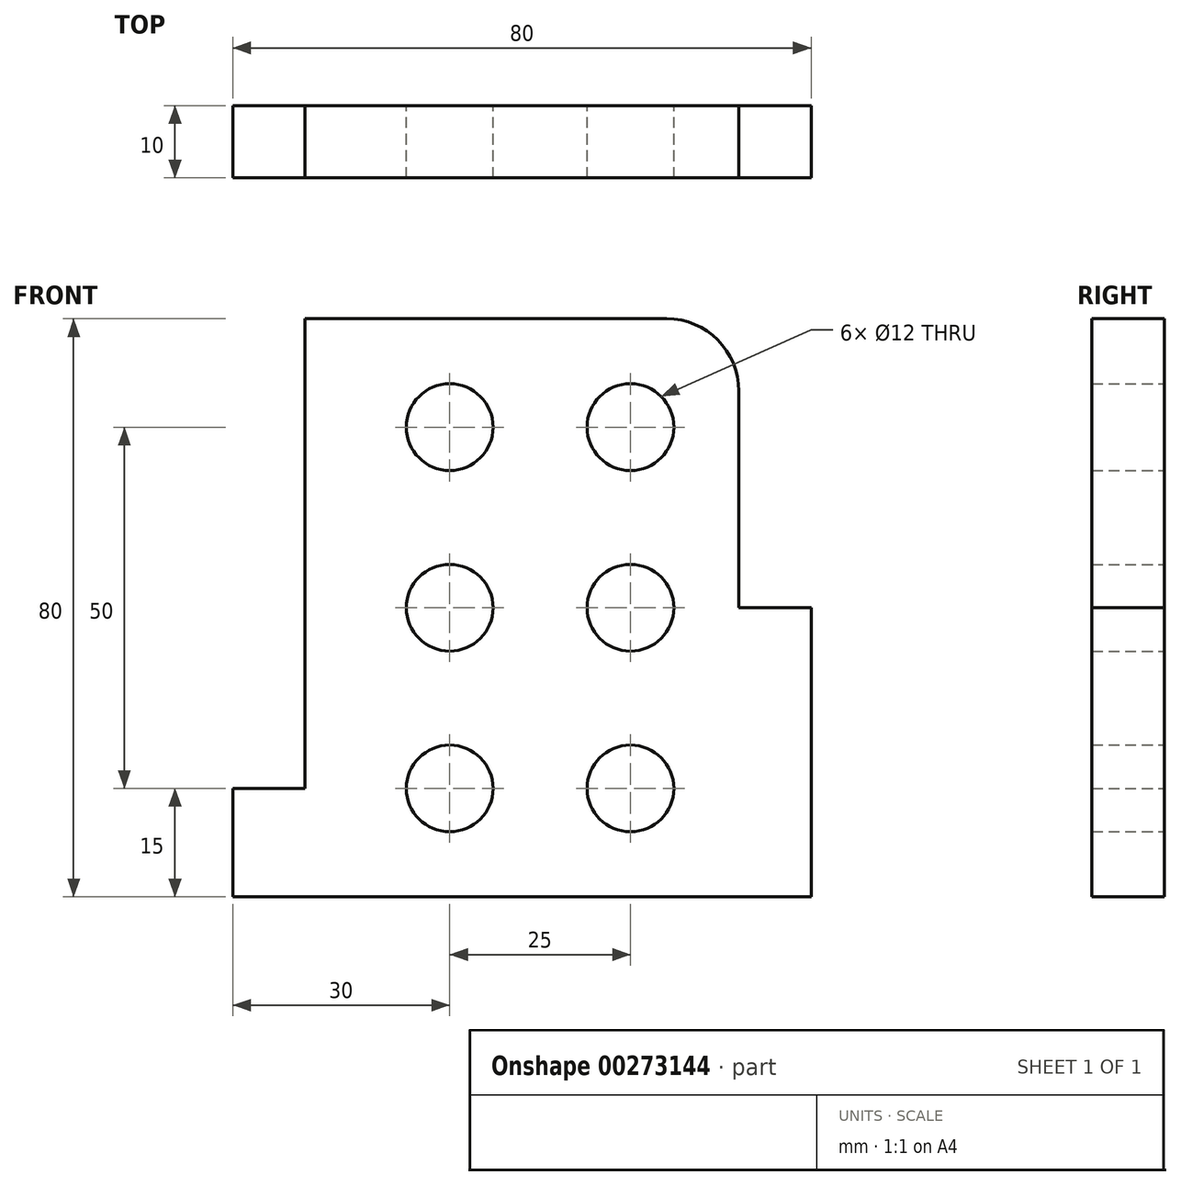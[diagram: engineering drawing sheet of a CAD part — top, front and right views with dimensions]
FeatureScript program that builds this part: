
annotation { "Feature Type Name" : "Feature", "Feature Type Description" : "" }
export const myFeature = defineFeature(function(context is Context, id is Id, definition is map)
    precondition{}
    {
        {
            var Q0;
            Q0=qCreatedBy(makeId("Front.planeOp"),FACE);
            var sketch = newSketch(context, id + "F0", { "sketchPlane" : qUnion([Q0])});
            skLineSegment(sketch, "E0", {"start": v(0, 0) * mm, "end": v(0, 15) * mm});
            skLineSegment(sketch, "E1", {"start": v(0, 15) * mm, "end": v(10, 15) * mm});
            skLineSegment(sketch, "E2", {"start": v(10, 15) * mm, "end": v(10, 80) * mm});
            skLineSegment(sketch, "E3", {"start": v(10, 80) * mm, "end": v(60, 80) * mm});
            skArc(sketch, "E4", {"start": v(60, 80) * mm, "mid": v(67.07, 77.07) * mm, "end": v(70, 70) * mm});
            skLineSegment(sketch, "E5", {"start": v(70, 70) * mm, "end": v(70, 40) * mm});
            skLineSegment(sketch, "E6", {"start": v(70, 40) * mm, "end": v(80, 40) * mm});
            skLineSegment(sketch, "E7", {"start": v(80, 40) * mm, "end": v(80, 0) * mm});
            skLineSegment(sketch, "E8", {"start": v(80, 0) * mm, "end": v(0, 0) * mm});
            skCircle(sketch, "E9", {"center": v(30, 65) * mm, "radius": 6 * mm});
            skCircle(sketch, "E10", {"center": v(55, 65) * mm, "radius": 6 * mm});
            skCircle(sketch, "E11", {"center": v(30, 40) * mm, "radius": 6 * mm});
            skCircle(sketch, "E12", {"center": v(55, 40) * mm, "radius": 6 * mm});
            skCircle(sketch, "E13", {"center": v(30, 15) * mm, "radius": 6 * mm});
            skCircle(sketch, "E14", {"center": v(55, 15) * mm, "radius": 6 * mm});
            skSolve(sketch);
        }
        {
            var Q0;
            Q0 = qSketchRegion(id + "F0", true);
            extrude(context, id + "F1", {"entities" : qUnion([Q0]), "depth" : 10 * mm});
        }
    });
